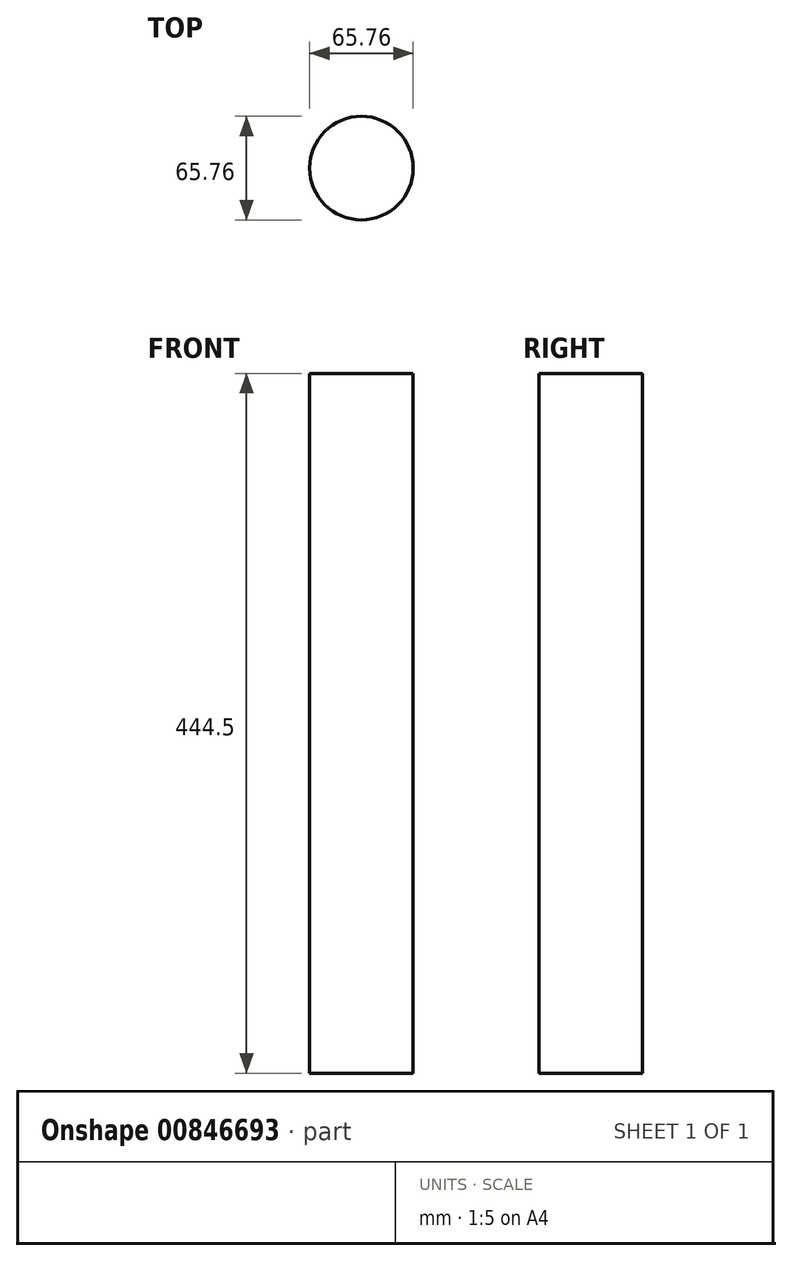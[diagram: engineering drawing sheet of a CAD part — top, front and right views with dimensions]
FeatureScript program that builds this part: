
annotation { "Feature Type Name" : "Feature", "Feature Type Description" : "" }
export const myFeature = defineFeature(function(context is Context, id is Id, definition is map)
    precondition{}
    {
        {
            var Q0;
            Q0=qCreatedBy(makeId("Top.planeOp"),FACE);
            var sketch = newSketch(context, id + "F0", { "sketchPlane" : qUnion([Q0])});
            skCircle(sketch, "E0", {"center": v(0, 0) * mm, "radius": 32.88 * mm});
            skSolve(sketch);
        }
        {
            var Q0;
            Q0=makeQuery(id+"F0.imprint","IMPRINT",FACE,{"disambiguationData":[TD([[makeQuery(id+"F0.imprint","IMPRINT",EDGE,{"derivedFrom":sQuery(id+"F0.wireOp",EDGE,"E0")}),1.0]])]});
            extrude(context, id + "F1", {"entities" : qUnion([Q0]), "depth" : 25.4 * mm, "offsetDistance" : 25.4 * mm});
        }
        {
            var Q0;
            Q0=makeQuery(id+"F1.opExtrude","CAP_FACE",FACE,{"disambiguationData":[OSD([sQuery(id+"F0.wireOp",EDGE,"E0")])],"isStart":false});
            var Q1;
            Q1=makeQuery(id+"F1.opExtrude","CAP_FACE",FACE,{"disambiguationData":[OSD([sQuery(id+"F0.wireOp",EDGE,"E0")])],"isStart":true});
            extrude(context, id + "F2", {"entities" : qUnion([Q0, Q1]), "operationType" : NewBodyOperationType.ADD, "depth" : 419.1 * mm, "offsetDistance" : 25.4 * mm});
        }
    });
